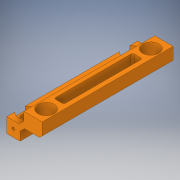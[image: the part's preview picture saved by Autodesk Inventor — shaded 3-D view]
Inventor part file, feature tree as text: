
AUTODESK INVENTOR PART (.ipt)
format: ipt  version: 2019 (Build 230136000, 136)  size: 239,616 bytes
history: native  units: in
note: dims shown in document units (in); Inventor stores cm internally (conversion verified against a paired STEP export)
features: sketch x8, extrude x5, hole x3, chamfer x2, fillet x1, projected_geometry x1
ambient origin geometry x8: Origin, YZ Plane, XZ Plane, XY Plane, X Axis, Y Axis, Z Axis, Center Point
bodies: Solid1 (feature_tree)
feature tree (20):
  extrude  "Extrusion1"  Depth=0.65in
  hole  "Hole2"  [1 undecoded]
  hole  "Hole3"  [1 undecoded]
  extrude  "Extrusion2"  Depth=0.25in
  extrude  "Extrusion3"  Depth=0.35in
  fillet  "Fillet1"  Radius=0.5in
  chamfer  "Chamfer1"  Distance=0.565in
  extrude  "Extrusion4"  Depth=0.7in
  extrude  "Extrusion5"  Depth=0.5in
  chamfer  "Chamfer2"  Distance=1.0in
  hole  "Hole4"  [1 undecoded]
  sketch  "Sketch1"  dims[d0=0.565in d2=0.65in]
  sketch  "Sketch3"  dims[d6=0.7in d9=0.85in]
  sketch  "Sketch4"  dims[d10=5.0in d11=0.0in d25=0.5in]
  sketch  "Sketch5"  dims[d26=0.5in d27=0.25in]
  sketch  "Sketch6"  dims[d28=0.25in]
  sketch  "Sketch7"  dims[d29=0.375in d30=0.75in d31=0.375in d32=0.25in d33=0.5635in d34=1.0in d35=0.8108in d36=0.35in d37=0.5in]
  sketch  "Sketch8"  dims[d38=0.5in]
  sketch  "Sketch9"  dims[d39=0.625in d40=0.75in d41=0.375in d42=0.25in d43=0.5635in d44=1.0in d45=0.8108in d47=0.565in d48=0.7in d49=0.5in d50=1.0in d51=0.175in d52=1.0in d53=0.375in d54=1.0in d55=0.0in d57=0.15in d58=0.15in d59=1.0in d60=0.0in d61=0.075in d62=0.17in d63=0.125in d64=45.0deg d65=0.64in d66=0.64in d67=0.15in d68=0.0in d69=0.15in d70=0.0in d71=0.1in d72=0.125in d73=45.0deg d74=0.565in d75=0.5in d76=0.2825in d77=0.25in d78=0.104in d79=0.75in d80=0.375in d81=0.25in d82=0.5635in d83=1.0in d84=0.8108in d18=1.0in d19=1.0in d20=1.0in d21=0.15in d22=0.25in d23=0.375in d24=0.5635in]
  projected_geometry  "Projected Loop1"
note: 3 required parameter values undecoded (feature->parameter linkage not recoverable at this tier; creation-order binding heuristic only, values carry confidence <= 0.55)
